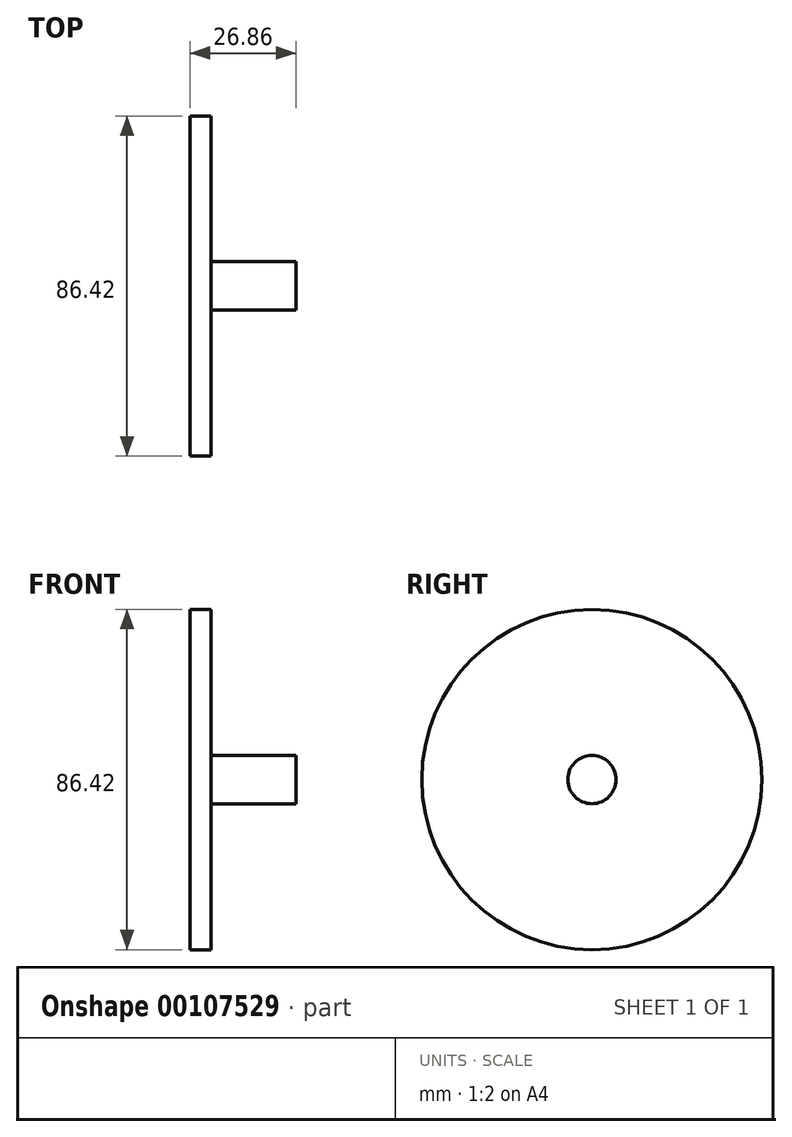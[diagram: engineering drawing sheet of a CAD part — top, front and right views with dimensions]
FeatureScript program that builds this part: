
annotation { "Feature Type Name" : "Feature", "Feature Type Description" : "" }
export const myFeature = defineFeature(function(context is Context, id is Id, definition is map)
    precondition{}
    {
        {
            var Q0;
            Q0=qCreatedBy(makeId("Front.planeOp"),FACE);
            var sketch = newSketch(context, id + "F0", { "sketchPlane" : qUnion([Q0])});
            skLineSegment(sketch, "E0", {"start": v(-54.01, 62.04) * mm, "end": v(-54.01, 18.83) * mm});
            skLineSegment(sketch, "E1", {"start": v(-54.01, 18.83) * mm, "end": v(-27.15, 18.83) * mm});
            skLineSegment(sketch, "E2", {"start": v(-27.15, 18.83) * mm, "end": v(-27.15, 24.96) * mm});
            skLineSegment(sketch, "E3", {"start": v(-27.15, 24.96) * mm, "end": v(-48.76, 24.96) * mm});
            skLineSegment(sketch, "E4", {"start": v(-48.76, 24.96) * mm, "end": v(-48.76, 62.04) * mm});
            skLineSegment(sketch, "E5", {"start": v(-48.76, 62.04) * mm, "end": v(-54.01, 62.04) * mm});
            skLineSegment(sketch, "E6", {"start": v(0, 0) * mm, "end": v(-26.13, 0) * mm});
            skLineSegment(sketch, "E7", {"start": v(-26.13, 0) * mm, "end": v(-27.15, 18.83) * mm});
            skSolve(sketch);
        }
        {
            var Q0;
            Q0=makeQuery(id+"F0.imprint","IMPRINT",FACE,{"disambiguationData":[TD([[makeQuery(id+"F0.imprint","IMPRINT",EDGE,{"derivedFrom":sQuery(id+"F0.wireOp",EDGE,"E0")}),1.0]])]});
            var Q1;
            Q1=sQuery(id+"F0.wireOp",EDGE,"E1");
            revolve(context, id + "F1", {"entities" : qUnion([Q0]), "axis" : qUnion([Q1]), "revolveType" : RevolveType.FULL});
        }
    });
